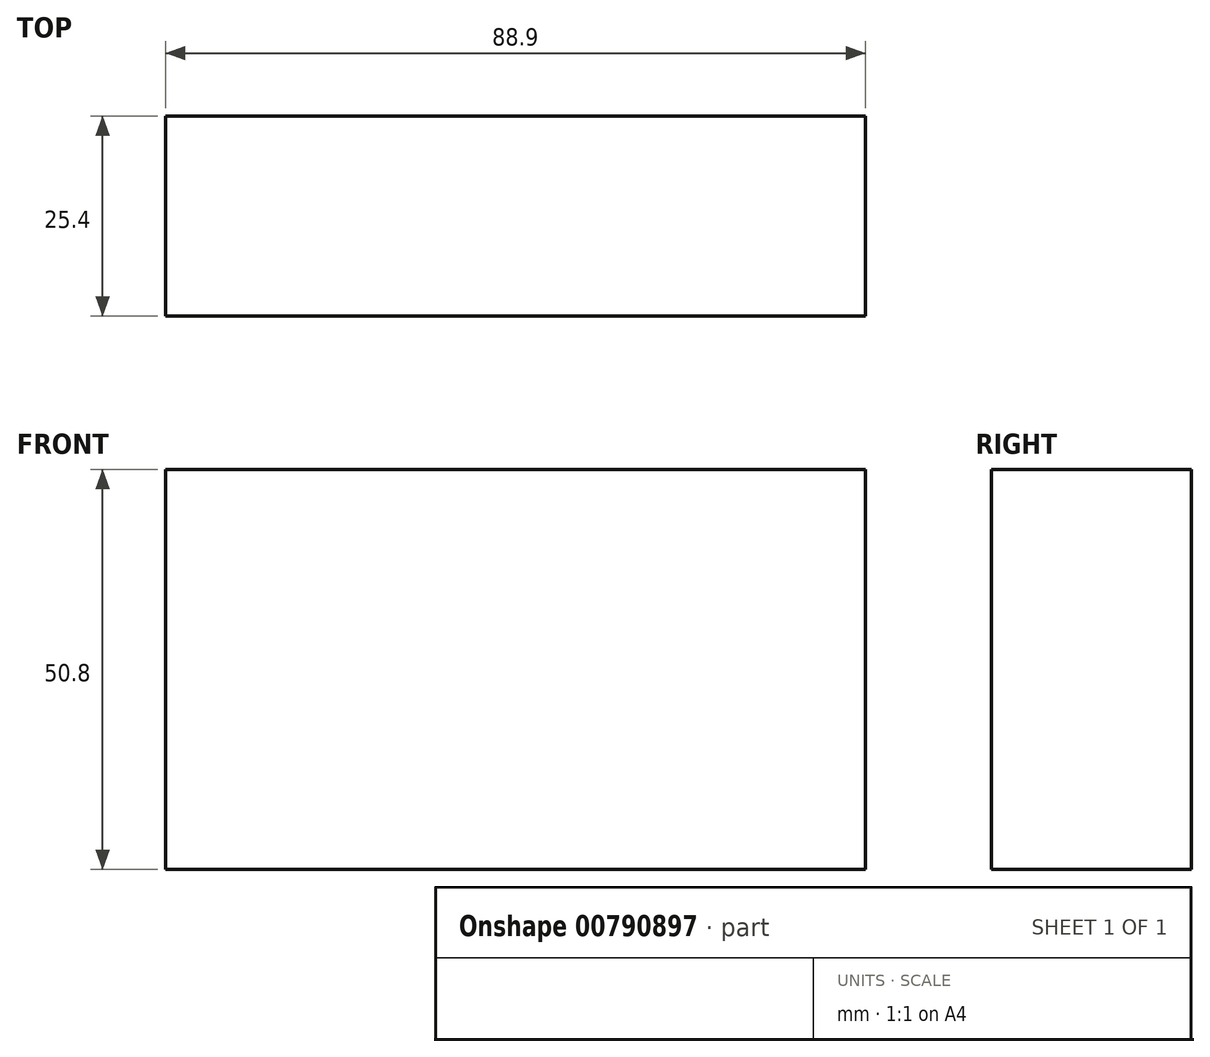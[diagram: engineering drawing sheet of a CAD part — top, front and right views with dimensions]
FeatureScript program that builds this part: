
annotation { "Feature Type Name" : "Feature", "Feature Type Description" : "" }
export const myFeature = defineFeature(function(context is Context, id is Id, definition is map)
    precondition{}
    {
        {
            var Q0;
            Q0=qCreatedBy(makeId("Top.planeOp"),FACE);
            var sketch = newSketch(context, id + "F0", { "sketchPlane" : qUnion([Q0])});
            skLineSegment(sketch, "E0.bottom", {"start": v(40.06, -21.38) * mm, "end": v(-48.84, -21.38) * mm});
            skLineSegment(sketch, "E0.top", {"start": v(40.06, 4.02) * mm, "end": v(-48.84, 4.02) * mm});
            skLineSegment(sketch, "E0.left", {"start": v(40.06, -21.38) * mm, "end": v(40.06, 4.02) * mm});
            skLineSegment(sketch, "E0.right", {"start": v(-48.84, -21.38) * mm, "end": v(-48.84, 4.02) * mm});
            skSolve(sketch);
        }
        {
            var Q0;
            Q0=makeQuery(id+"F0.imprint","IMPRINT",FACE,{"disambiguationData":[TD([[makeQuery(id+"F0.imprint","IMPRINT",EDGE,{"derivedFrom":sQuery(id+"F0.wireOp",EDGE,"E0.bottom")}),-1.0]])]});
            extrude(context, id + "F1", {"entities" : qUnion([Q0]), "depth" : 50.8 * mm, "offsetDistance" : 25.4 * mm});
        }
    });
